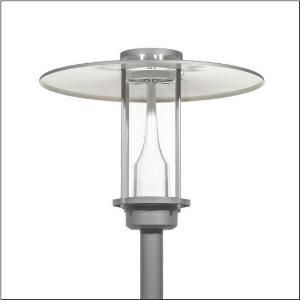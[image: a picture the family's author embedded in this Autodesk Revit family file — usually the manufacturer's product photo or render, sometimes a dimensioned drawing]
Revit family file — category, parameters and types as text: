
# Revit family: city-light_plus_iq___st1_2a_5xa5275kf14hp_140d
name_source: partatom
category: Lighting Fixtures
units: mm (PartAtom-declared; Revit-internal decimal feet)

## family parameters
Cut with Voids When Loaded = No
Host = Face
Light Source = No
Part Type = Normal
Room Calculation Point = No
Round Connector Dimension = Use Diameter
Shared = No

## types (1)
- --- (1 x LED, 4710 lm, 33.6 W, 4000K)
    Apparent Load = 34 VA
    CIE Flux Codes = 22 60 93 97 100
    Color Rendering = 70
    Color Temperature = 4000K
    Default Elevation = 1800 mm
    Description = City-Light Plus iQ, mast luminaire, Module 540 iQ-SR, primary light control with 3 zone facetted reflector, of plastic, silver coated, highly specular, structured, primary optical cover: cover, of PMMA, transparent, light distribution: ST1.2a, light emission: direct distribution, primary light characteristic: asymmetric, installation type: post-top, LED, High Power LED, rated luminous flux: 4.710lm, luminous efficacy: 140lm/W, light colour: 740, colour temperature: 4000K, control gear: iQ Street-Remote, control: pre-setting: logarithmic dimming characteristic, Street-Remote, Auto-Match, Temp-Guard, Lumen-Switch, Night-Set, Smart-Wire, Light-Fading, Desk-Remote (wireless, voltage-free reading and setting of iQ features in the workshop via application-optimized NFC function/RFID function), optimised constant luminous flux control (CLO 2.0), with terminal, 6-pole, max. 2.5mm², mains connection: 230..240V, AC, 50/60Hz, start of lifetime: 34W, end of service life: 36W, reduction: 15W, luminaire housing, upper part, of glass-fibre reinforced polyester, coated, Siteco® metallic grey (DB 702S), diameter: 750mm, height: 590mm, spigot size: d x l = 76 x 70mm (post-top) | with reducer (optional accessory) 60 x 70mm, mounting height: 3..5m, post-top mast mounting element, of diecast aluminium, coated, Siteco® metallic grey (DB 702S), Module 540 iQ-SR, traffic white (RAL 9016), equipment: Power, protection rating (complete): IP65, insulation class (complete): insulation class II (safety insulation), certification: CE, ENEC, VDE, packaging unit: 1 piece

Light Distribution: ST1.2a
    Height = 590 mm
    Lamp = 1 x LED
    Lamp Light Flux = 4710 lm
    Lamp Power = 33.6 W
    Lamp count = 1
    Length = 750 mm
    Luminous efficacy = 140 lm/W
    Manufacturer = Siteco
    ModVariant = No
    Model = 5XA5275KF14HP
    Mounting Place = Pole
    Mounting Type = Pole top
    Number of Poles = 1
    OnlyDefault = Yes
    Power Factor = 1
    Product Name = City-Light Plus iQ | ST1.2a
    Product group = mast luminaire | pylon top
    ProductGroupID = 6100
    Protection Class = Protection class II
    Protection Degree = IP 65
    RLX_Detail_Level = 1
    RLX_Emergency_Light_Flux = 0 lm
    RLX_Emergency_Type = 0
    RLX_Emergency_Type_DB = No
    RlxData = <blob elided: 52613 chars, md5=13fca444>
    Socket = socket
    Standby Power = 0 W
    System Light Flux = 4710 lm
    System Power = 34 W
    Type Comments = factory setting: luminous flux: 100 % | dim-lin: 254 | 695 mA
    Type Image = l_1006456.jpg
    URL = http://relux.com
    VarID = @adj_192831
    Voltage = 0 V
    Weight = 0.00 kg
    Width = 0 mm  [stored 0 ft]

note: [stored X ft] marks values corroborated as IEEE doubles in the binary element streams (Revit-internal decimal feet)

## geometry (parser evidence)
native form markers: Blend x4, Sweep x13
no freeform markers — native parametric forms only
